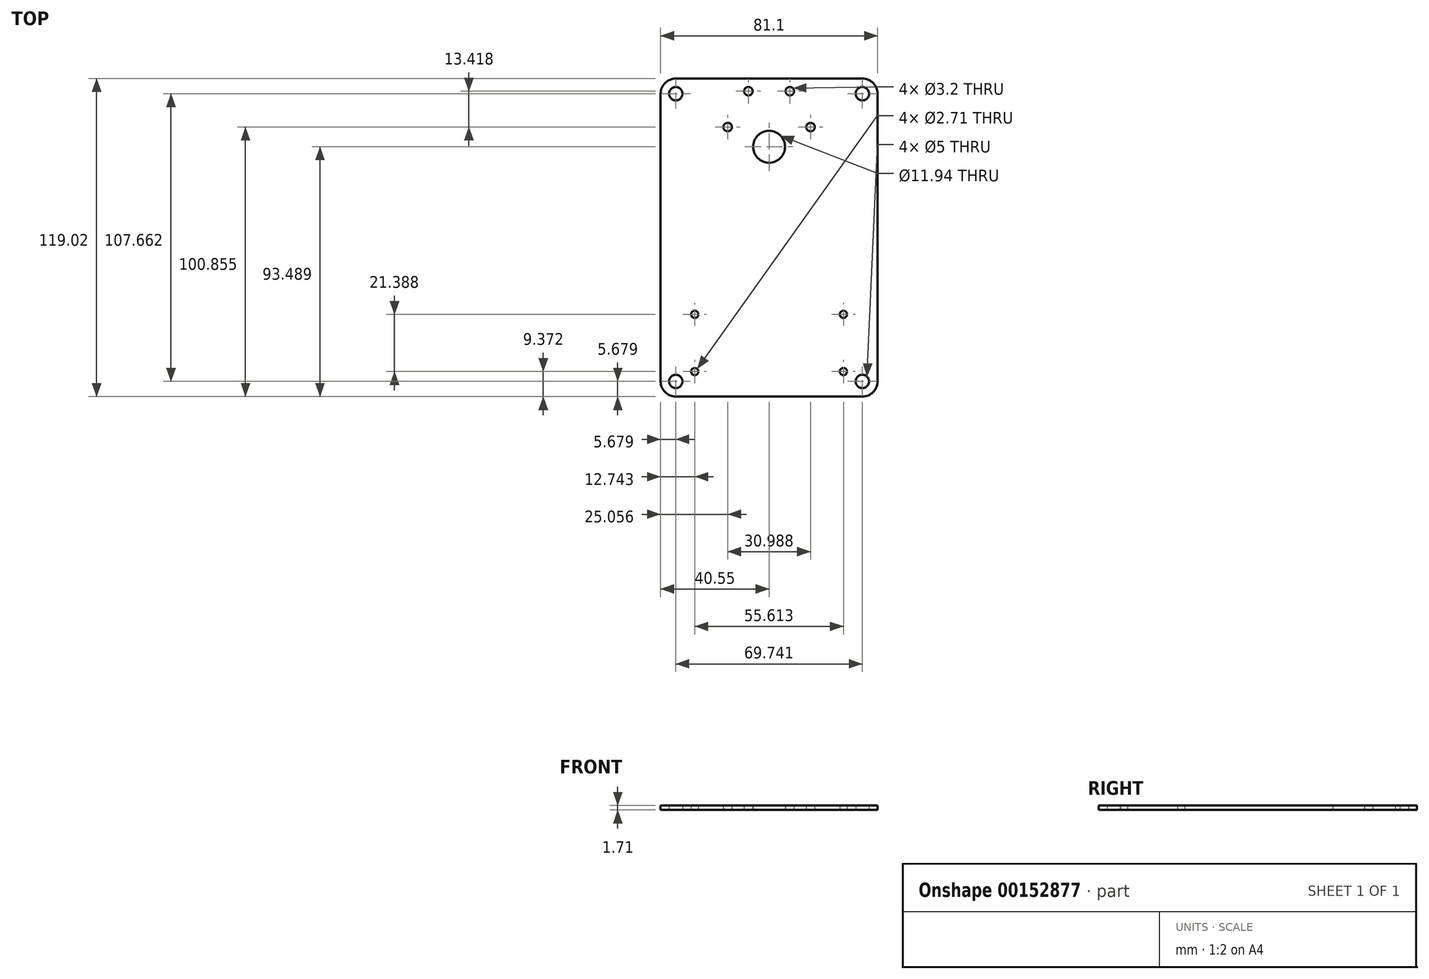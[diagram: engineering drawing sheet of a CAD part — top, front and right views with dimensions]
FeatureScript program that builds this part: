
annotation { "Feature Type Name" : "Feature", "Feature Type Description" : "" }
export const myFeature = defineFeature(function(context is Context, id is Id, definition is map)
    precondition{}
    {
        {
            var Q0;
            Q0=qCreatedBy(makeId("Top.planeOp"),FACE);
            var sketch = newSketch(context, id + "F0", { "sketchPlane" : qUnion([Q0])});
            skLineSegment(sketch, "E0.bottom", {"start": v(34.87, 53.83) * mm, "end": v(-34.87, 53.83) * mm, "construction": true});
            skLineSegment(sketch, "E0.top", {"start": v(34.87, -53.83) * mm, "end": v(-34.87, -53.83) * mm, "construction": true});
            skLineSegment(sketch, "E0.left", {"start": v(34.87, 53.83) * mm, "end": v(34.87, -53.83) * mm, "construction": true});
            skLineSegment(sketch, "E0.right", {"start": v(-34.87, 53.83) * mm, "end": v(-34.87, -53.83) * mm, "construction": true});
            skPoint(sketch, "E0.middle", {"position": v(0, 0) * mm});
            skLineSegment(sketch, "E1.bottom", {"start": v(40.55, 59.5) * mm, "end": v(-40.55, 59.5) * mm});
            skLineSegment(sketch, "E1.top", {"start": v(40.55, -59.5) * mm, "end": v(-40.55, -59.5) * mm});
            skLineSegment(sketch, "E1.left", {"start": v(40.55, 59.5) * mm, "end": v(40.55, -59.5) * mm});
            skLineSegment(sketch, "E1.right", {"start": v(-40.55, 59.5) * mm, "end": v(-40.55, -59.5) * mm});
            skLineSegment(sketch, "E2", {"start": v(34.87, 53.83) * mm, "end": v(34.87, 59.5) * mm, "construction": true});
            skLineSegment(sketch, "E3", {"start": v(34.87, 53.83) * mm, "end": v(40.55, 53.83) * mm, "construction": true});
            skCircle(sketch, "E4", {"center": v(-34.87, 53.83) * mm, "radius": 2.5 * mm});
            skCircle(sketch, "E5", {"center": v(34.87, 53.83) * mm, "radius": 2.5 * mm});
            skCircle(sketch, "E6", {"center": v(34.87, -53.83) * mm, "radius": 2.5 * mm});
            skCircle(sketch, "E7", {"center": v(-34.87, -53.83) * mm, "radius": 2.5 * mm});
            skLineSegment(sketch, "E8", {"start": v(27.8, -50.14) * mm, "end": v(27.8, -28.75) * mm, "construction": true});
            skLineSegment(sketch, "E9", {"start": v(27.8, -28.75) * mm, "end": v(-27.8, -28.75) * mm, "construction": true});
            skLineSegment(sketch, "E10", {"start": v(-27.8, -28.75) * mm, "end": v(-27.8, -50.14) * mm, "construction": true});
            skLineSegment(sketch, "E11", {"start": v(0, 0) * mm, "end": v(0, -28.75) * mm, "construction": true});
            skCircle(sketch, "E12", {"center": v(27.8, -50.14) * mm, "radius": 1.35 * mm});
            skCircle(sketch, "E13", {"center": v(27.8, -28.75) * mm, "radius": 1.35 * mm});
            skCircle(sketch, "E14", {"center": v(-27.8, -28.75) * mm, "radius": 1.35 * mm});
            skCircle(sketch, "E15", {"center": v(-27.8, -50.14) * mm, "radius": 1.35 * mm});
            skLineSegment(sketch, "E16", {"start": v(0, -28.75) * mm, "end": v(0, -50.14) * mm, "construction": true});
            skLineSegment(sketch, "E17", {"start": v(0, -50.14) * mm, "end": v(0, -53.83) * mm, "construction": true});
            skCircle(sketch, "E18", {"center": v(0, 41.34) * mm, "radius": 18.16 * mm, "construction": true});
            skLineSegment(sketch, "E19", {"start": v(0, 41.34) * mm, "end": v(0, 0) * mm, "construction": true});
            skCircle(sketch, "E20.cCircle", {"center": v(0, 41.34) * mm, "radius": 13.42 * mm, "construction": true});
            skLineSegment(sketch, "E20.0", {"start": v(7.75, 27.93) * mm, "end": v(-7.75, 27.93) * mm, "construction": true});
            skLineSegment(sketch, "E20.1", {"start": v(-7.75, 27.93) * mm, "end": v(-15.5, 41.34) * mm, "construction": true});
            skLineSegment(sketch, "E20.2", {"start": v(-15.5, 41.34) * mm, "end": v(-7.75, 54.76) * mm, "construction": true});
            skLineSegment(sketch, "E20.3", {"start": v(-7.75, 54.76) * mm, "end": v(7.75, 54.76) * mm, "construction": true});
            skLineSegment(sketch, "E20.4", {"start": v(7.75, 54.76) * mm, "end": v(15.5, 41.34) * mm, "construction": true});
            skLineSegment(sketch, "E20.5", {"start": v(15.5, 41.34) * mm, "end": v(7.75, 27.93) * mm, "construction": true});
            skPoint(sketch, "E20.0.midPoint", {"position": v(0, 27.93) * mm});
            skCircle(sketch, "E21", {"center": v(-15.5, 41.34) * mm, "radius": 1.6 * mm});
            skCircle(sketch, "E22", {"center": v(15.5, 41.34) * mm, "radius": 1.6 * mm});
            skCircle(sketch, "E23", {"center": v(7.75, 27.93) * mm, "radius": 1.6 * mm, "construction": true});
            skCircle(sketch, "E24", {"center": v(7.75, 54.76) * mm, "radius": 1.6 * mm});
            skCircle(sketch, "E25", {"center": v(-7.75, 54.76) * mm, "radius": 1.6 * mm});
            skCircle(sketch, "E26", {"center": v(-7.75, 27.93) * mm, "radius": 1.6 * mm, "construction": true});
            skCircle(sketch, "E27", {"center": v(0, 33.98) * mm, "radius": 5.97 * mm});
            skSolve(sketch);
        }
        {
            var Q0;
            Q0 = qSketchRegion(id + "F0", true);
            extrude(context, id + "F1", {"entities" : qUnion([Q0]), "depth" : 1.7 * mm});
        }
        {
            var Q0;
            Q0=makeQuery(id+"F1.opExtrude","SWEPT_EDGE",EDGE,{"disambiguationData":[OSD([sQuery(id+"F0.wireOp",EDGE,"E1.bottom"),sQuery(id+"F0.wireOp",EDGE,"E1.left")])]});
            var Q1;
            Q1=makeQuery(id+"F1.opExtrude","SWEPT_EDGE",EDGE,{"disambiguationData":[OSD([sQuery(id+"F0.wireOp",EDGE,"E1.top"),sQuery(id+"F0.wireOp",EDGE,"E1.left")])]});
            var Q2;
            Q2=makeQuery(id+"F1.opExtrude","SWEPT_EDGE",EDGE,{"disambiguationData":[OSD([sQuery(id+"F0.wireOp",EDGE,"E1.top"),sQuery(id+"F0.wireOp",EDGE,"E1.right")])]});
            var Q3;
            Q3=makeQuery(id+"F1.opExtrude","SWEPT_EDGE",EDGE,{"disambiguationData":[OSD([sQuery(id+"F0.wireOp",EDGE,"E1.bottom"),sQuery(id+"F0.wireOp",EDGE,"E1.right")])]});
            fillet(context, id + "F2", {"entities" : qUnion([Q0, Q1, Q2, Q3]), "radius" : 5.67 * mm, "tangentPropagation" : true, "allowEdgeOverflow" : false});
        }
    });
